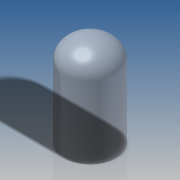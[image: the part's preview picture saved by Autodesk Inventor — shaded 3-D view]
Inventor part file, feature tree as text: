
AUTODESK INVENTOR PART (.ipt)
format: ipt  version: 2016 SP2 (Build 200236200, 236)  size: 141,824 bytes
history: native  units: in
note: dims shown in document units (in); Inventor stores cm internally (conversion verified against a paired STEP export)
features: revolve x1, sketch x1
ambient origin geometry x8: Origin, YZ Plane, XZ Plane, XY Plane, X Axis, Y Axis, Z Axis, Center Point
bodies: Solid1 (feature_tree)
feature tree (2):
  revolve  "Revolution1"  [1 undecoded]
  sketch  "Sketch2"  dims[d0=0.126in d1=0.1732in d2=0.0472in d3=90.0deg]
note: 1 required parameter value undecoded (feature->parameter linkage not recoverable at this tier; creation-order binding heuristic only, values carry confidence <= 0.55)
